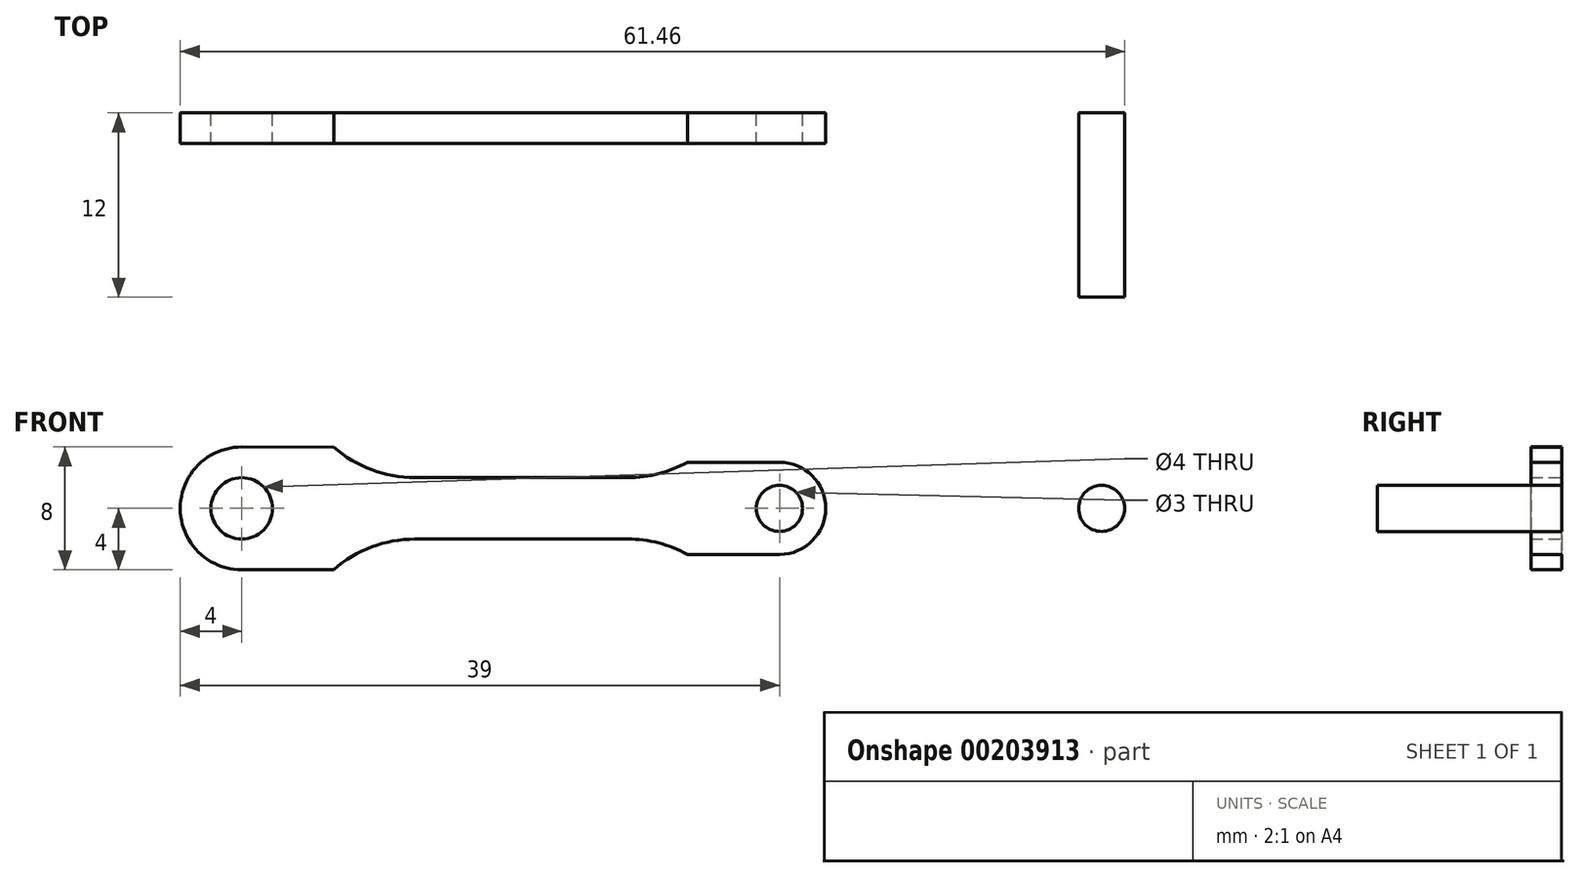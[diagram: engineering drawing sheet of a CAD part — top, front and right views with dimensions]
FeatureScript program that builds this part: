
annotation { "Feature Type Name" : "Feature", "Feature Type Description" : "" }
export const myFeature = defineFeature(function(context is Context, id is Id, definition is map)
    precondition{}
    {
        {
            var Q0;
            Q0=qCreatedBy(makeId("Front.planeOp"),FACE);
            var sketch = newSketch(context, id + "F0", { "sketchPlane" : qUnion([Q0])});
            skCircle(sketch, "E0", {"center": v(-17.5, 0) * mm, "radius": 2 * mm});
            skCircle(sketch, "E1", {"center": v(17.5, 0) * mm, "radius": 1.5 * mm});
            skCircle(sketch, "E2.0", {"center": v(17.5, 0) * mm, "radius": 3 * mm});
            skLineSegment(sketch, "E3", {"start": v(-6.23, 2) * mm, "end": v(7.63, 2) * mm});
            skArc(sketch, "E4", {"start": v(-6.23, 2) * mm, "mid": v(-9.04, 2.51) * mm, "end": v(-11.5, 3.98) * mm});
            skArc(sketch, "E5", {"start": v(7.63, 2) * mm, "mid": v(9.63, 2.25) * mm, "end": v(11.5, 3) * mm});
            skLineSegment(sketch, "E6", {"start": v(17.5, 0) * mm, "end": v(17.5, 7.2) * mm, "construction": true});
            skLineSegment(sketch, "E7", {"start": v(17.5, 3) * mm, "end": v(11.5, 3) * mm});
            skCircle(sketch, "E8", {"center": v(-17.5, 0) * mm, "radius": 4 * mm});
            skLineSegment(sketch, "E9", {"start": v(-17.5, 4) * mm, "end": v(-11.5, 3.98) * mm});
            skLineSegment(sketch, "E10.MirrorCS", {"start": v(-6.23, -2) * mm, "end": v(7.63, -2) * mm});
            skArc(sketch, "E11.MirrorCS", {"start": v(7.63, -2) * mm, "mid": v(9.63, -2.25) * mm, "end": v(11.5, -3) * mm});
            skLineSegment(sketch, "E12.MirrorCS", {"start": v(17.5, -3) * mm, "end": v(11.5, -3) * mm});
            skLineSegment(sketch, "E13.MirrorCS", {"start": v(-17.5, -4) * mm, "end": v(-11.5, -3.98) * mm});
            skArc(sketch, "E14.MirrorCS", {"start": v(-6.23, -2) * mm, "mid": v(-9.04, -2.51) * mm, "end": v(-11.5, -3.98) * mm});
            skSolve(sketch);
        }
        {
            var Q0;
            Q0=qSketchRegion(id+"F0",true);
            extrude(context, id + "F1", {"entities" : qUnion([Q0]), "depth" : 2 * mm});
        }
        {
            var Q0;
            Q0=qCreatedBy(makeId("Front.planeOp"),FACE);
            var sketch = newSketch(context, id + "F2", { "sketchPlane" : qUnion([Q0])});
            skCircle(sketch, "E15", {"center": v(38.46, 0) * mm, "radius": 1.5 * mm});
            skSolve(sketch);
        }
        {
            var Q0;
            Q0=qSketchRegion(id+"F2",true);
            extrude(context, id + "F3", {"entities" : qUnion([Q0]), "depth" : 12 * mm});
        }
    });
